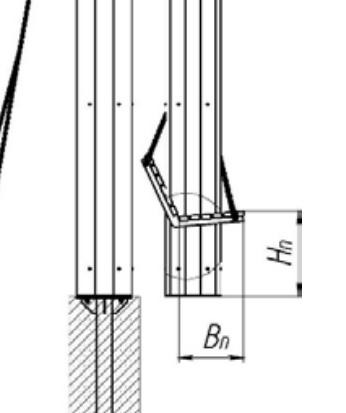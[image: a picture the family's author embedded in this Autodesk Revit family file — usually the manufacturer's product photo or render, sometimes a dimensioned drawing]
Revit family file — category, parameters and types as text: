
# Revit family: 14001 Диван-качели «Олимпия» Хоббика
name_source: partatom
category: Антураж
revit_build: Autodesk Revit 2018 (Build: 20180423_1000(x64)
units: mm (PartAtom-declared; Revit-internal decimal feet)

## family parameters
Всегда вертикально = Да
Источник визуального образа = Геометрия семейства
На основе рабочей плоскости = Нет
Общий = Нет
При загрузке вырезать с полостями = Нет
Точка расчета площади = Нет

## types (2) — shared parameters
URL = https://hobbyka.ru
Артикул товара = Арт. 14001
Высота = 2800 мм
Группа модели = Парковые качели
Длина = 3360 мм
Изготовитель = ООО «Хоббика»
Изображение типоразмера = Диван-качели «Олимпия» Арт 14001.jpg
Материал изделия = Сталь, дерево
Цвет каркаса = Сталь
Ширина = 665 мм

## per-type parameters (varying)
| type | Ангарская сосна | Лиственница | Описание | Цвет отделки |
| Версия "Ангарская сосна" | Да | Нет | Диван-качели «Олимпия». Версия Ангарская сосна | Ангарская сосна |
| Версия "Лиственница" | Нет | Да | Диван-качели «Олимпия». Версия Лиственница | Лиственница |
